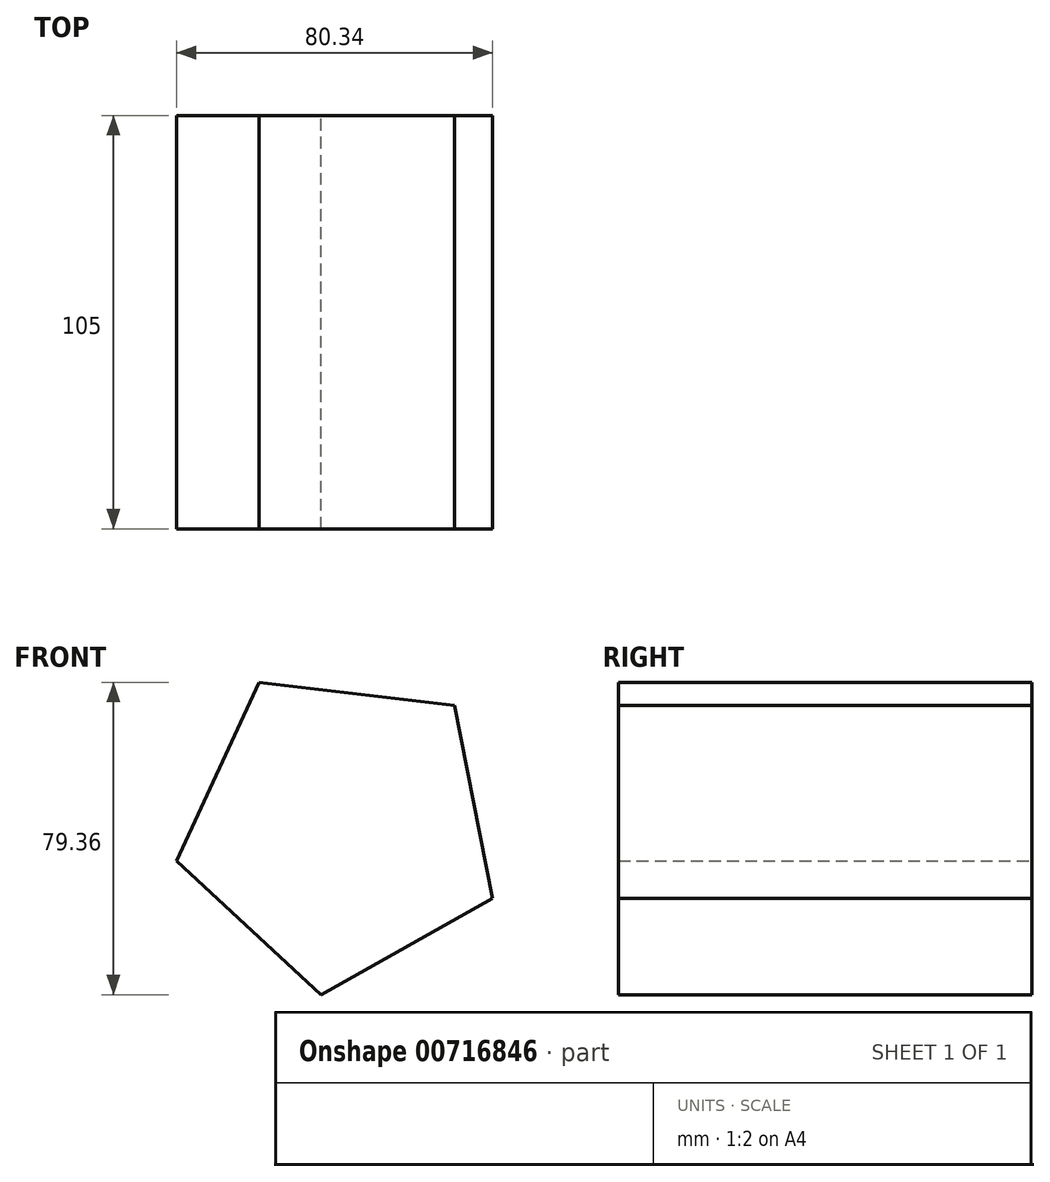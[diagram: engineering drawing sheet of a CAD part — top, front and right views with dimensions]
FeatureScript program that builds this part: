
annotation { "Feature Type Name" : "Feature", "Feature Type Description" : "" }
export const myFeature = defineFeature(function(context is Context, id is Id, definition is map)
    precondition{}
    {
        {
            var Q0;
            Q0=qCreatedBy(makeId("Front.planeOp"),FACE);
            var sketch = newSketch(context, id + "F0", { "sketchPlane" : qUnion([Q0])});
            skCircle(sketch, "E0.cCircle", {"center": v(0, 0) * mm, "radius": 34.4 * mm, "construction": true});
            skLineSegment(sketch, "E0.0", {"start": v(38.62, -17.83) * mm, "end": v(-5.02, -42.24) * mm});
            skLineSegment(sketch, "E0.1", {"start": v(-5.02, -42.24) * mm, "end": v(-41.72, -8.28) * mm});
            skLineSegment(sketch, "E0.2", {"start": v(-41.72, -8.28) * mm, "end": v(-20.76, 37.12) * mm});
            skLineSegment(sketch, "E0.3", {"start": v(-20.76, 37.12) * mm, "end": v(28.89, 31.22) * mm});
            skLineSegment(sketch, "E0.4", {"start": v(28.89, 31.22) * mm, "end": v(38.62, -17.83) * mm});
            skPoint(sketch, "E0.0.midPoint", {"position": v(16.8, -30.03) * mm});
            skSolve(sketch);
        }
        {
            var Q0;
            Q0 = qSketchRegion(id + "F0", true);
            extrude(context, id + "F1", {"entities" : qUnion([Q0]), "depth" : 105 * mm, "offsetDistance" : 25 * mm});
        }
    });
